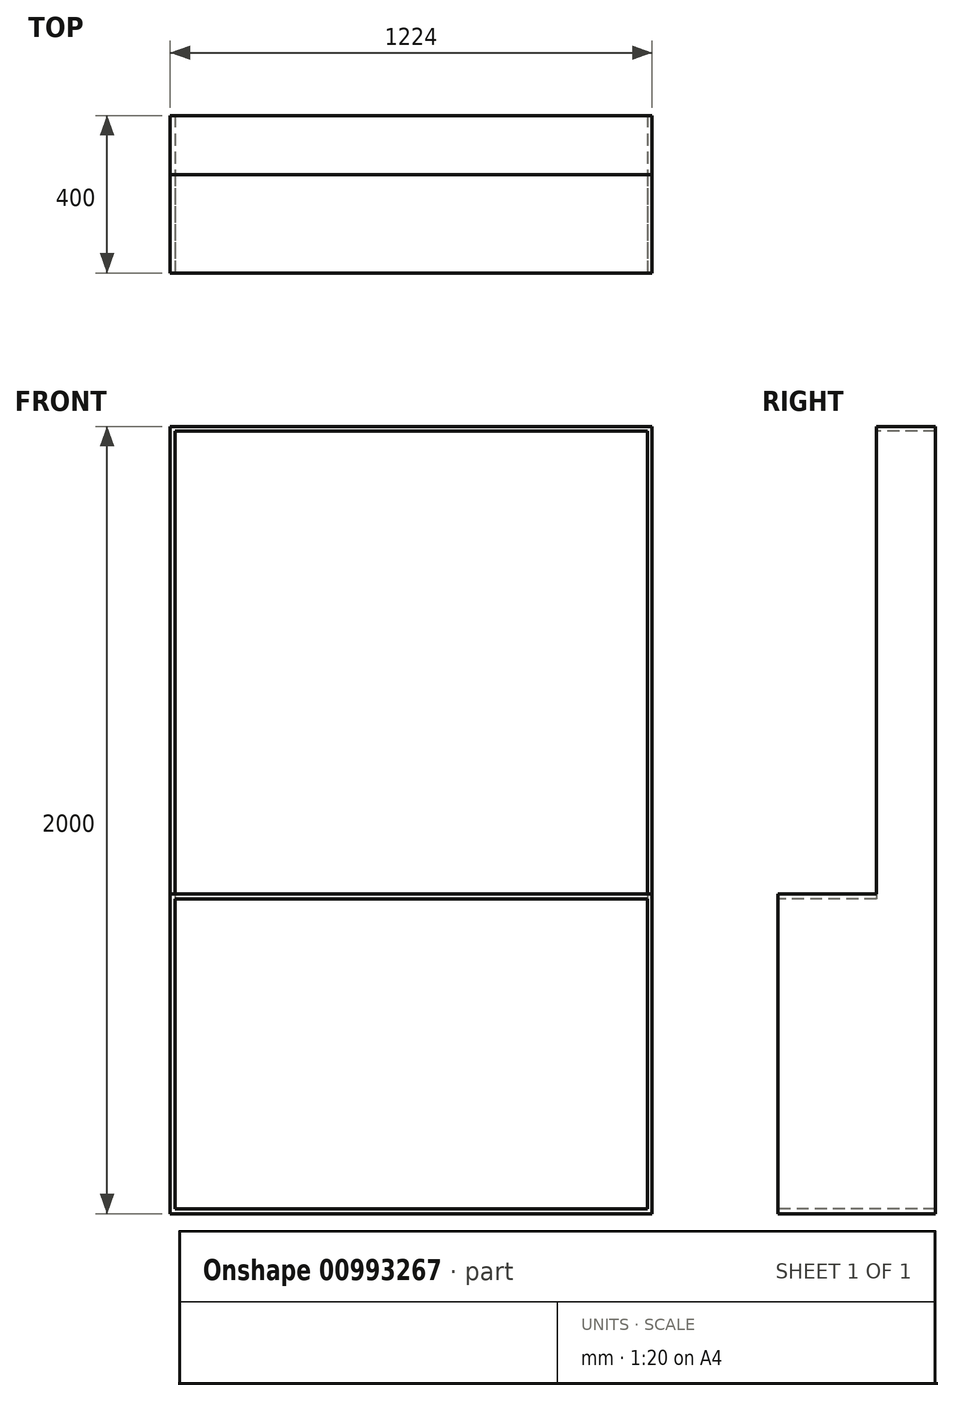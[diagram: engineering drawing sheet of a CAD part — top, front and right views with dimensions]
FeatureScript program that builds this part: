
annotation { "Feature Type Name" : "Feature", "Feature Type Description" : "" }
export const myFeature = defineFeature(function(context is Context, id is Id, definition is map)
    precondition{}
    {
        {
            var Q0;
            Q0=qCreatedBy(makeId("Top.planeOp"),FACE);
            var sketch = newSketch(context, id + "F0", { "sketchPlane" : qUnion([Q0])});
            skLineSegment(sketch, "E0.bottom", {"start": v(612, 200) * mm, "end": v(-612, 200) * mm});
            skLineSegment(sketch, "E0.top", {"start": v(612, -200) * mm, "end": v(-612, -200) * mm});
            skLineSegment(sketch, "E0.left", {"start": v(612, 200) * mm, "end": v(612, -200) * mm});
            skLineSegment(sketch, "E0.right", {"start": v(-612, 200) * mm, "end": v(-612, -200) * mm});
            skPoint(sketch, "E0.middle", {"position": v(0, 0) * mm});
            skSolve(sketch);
        }
        {
            var Q0;
            Q0 = qSketchRegion(id + "F0", true);
            extrude(context, id + "F1", {"entities" : qUnion([Q0]), "depth" : 2000 * mm, "offsetDistance" : 25 * mm});
        }
        {
            var Q0;
            Q0=makeQuery(id+"F1.opExtrude","SWEPT_FACE",FACE,{"disambiguationData":[OSD([sQuery(id+"F0.wireOp",EDGE,"E0.top")])]});
            var sketch = newSketch(context, id + "F2", { "sketchPlane" : qUnion([Q0])});
            skLineSegment(sketch, "E1.bottom", {"start": v(-612, 2000) * mm, "end": v(612, 2000) * mm});
            skLineSegment(sketch, "E1.top", {"start": v(-612, 812) * mm, "end": v(612, 812) * mm});
            skLineSegment(sketch, "E1.left", {"start": v(-612, 2000) * mm, "end": v(-612, 812) * mm});
            skLineSegment(sketch, "E1.right", {"start": v(612, 2000) * mm, "end": v(612, 812) * mm});
            skSolve(sketch);
        }
        {
            var Q0;
            Q0 = qSketchRegion(id + "F2", true);
            extrude(context, id + "F3", {"entities" : qUnion([Q0]), "operationType" : NewBodyOperationType.REMOVE, "oppositeDirection" : true, "depth" : 250 * mm, "offsetDistance" : 25 * mm});
        }
        {
            var Q0;
            Q0=makeQuery(id+"F1.opExtrude","SWEPT_FACE",FACE,{"disambiguationData":[OSD([sQuery(id+"F0.wireOp",EDGE,"E0.bottom")])]});
            var Q1;
            Q1=makeQuery(id+"F3.boolean.opBoolean","COPY",FACE,{"derivedFrom":makeQuery(id+"F3.opExtrude","CAP_FACE",FACE,{"disambiguationData":[OSD([sQuery(id+"F2.wireOp",EDGE,"E1.bottom"),sQuery(id+"F2.wireOp",EDGE,"E1.top"),sQuery(id+"F2.wireOp",EDGE,"E1.left"),sQuery(id+"F2.wireOp",EDGE,"E1.right")])],"isStart":false})});
            var Q2;
            Q2=makeQuery(id+"F1.opExtrude","SWEPT_FACE",FACE,{"disambiguationData":[OSD([sQuery(id+"F0.wireOp",EDGE,"E0.top")])]});
            shell(context, id + "F4", {"entities" : qUnion([Q0, Q1, Q2]), "thickness" : 12 * mm});
        }
    });
